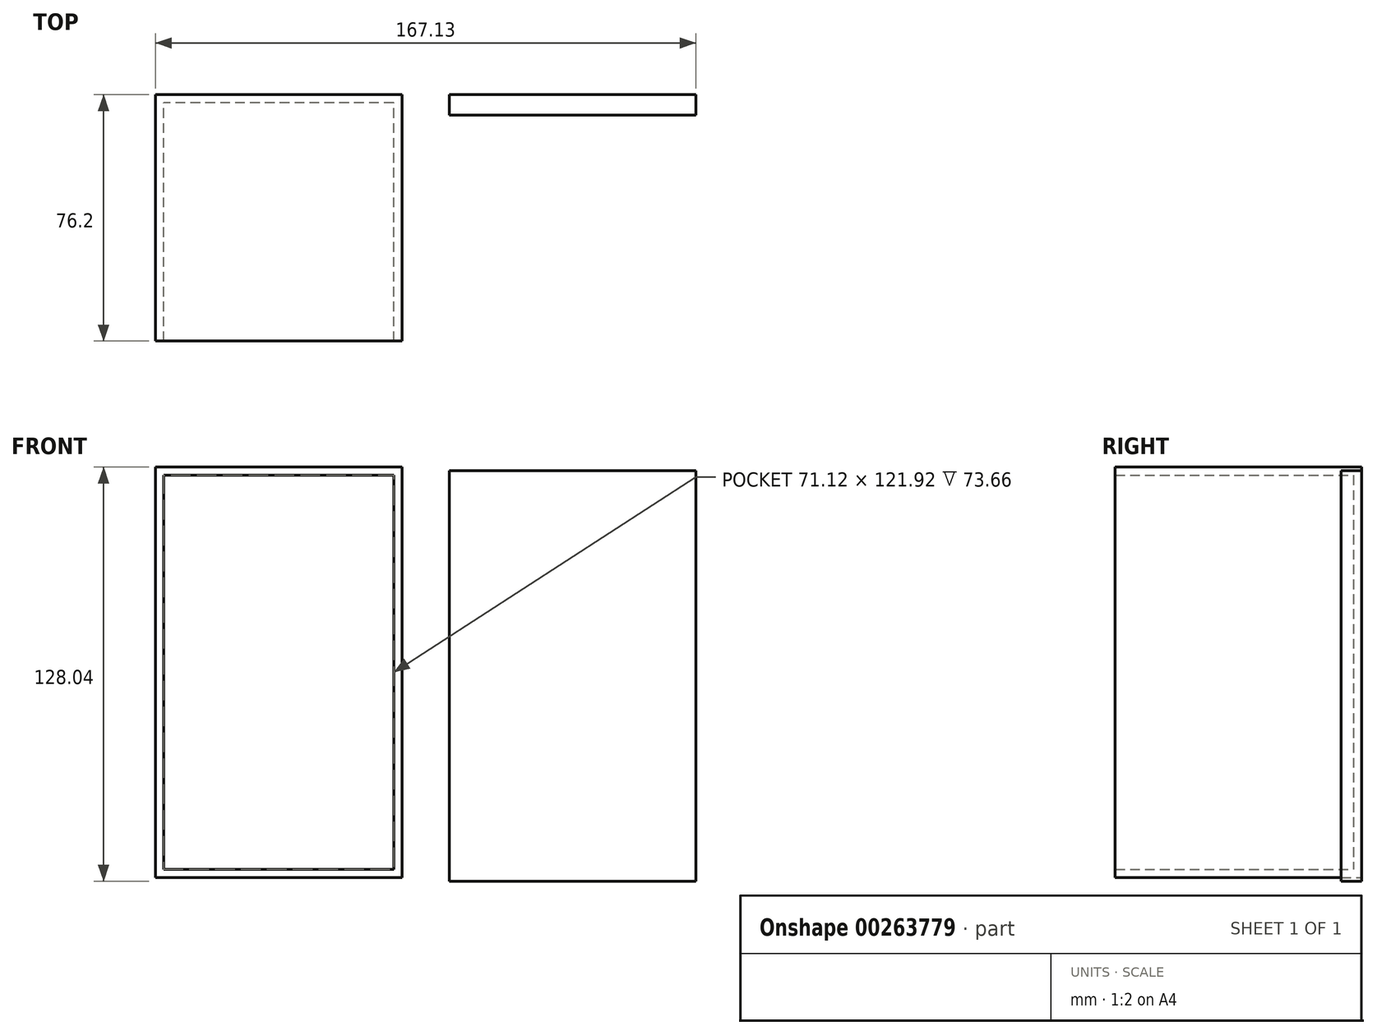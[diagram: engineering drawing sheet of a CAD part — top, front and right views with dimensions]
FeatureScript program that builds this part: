
annotation { "Feature Type Name" : "Feature", "Feature Type Description" : "" }
export const myFeature = defineFeature(function(context is Context, id is Id, definition is map)
    precondition{}
    {
        {
            var Q0;
            Q0=qCreatedBy(makeId("Front.planeOp"),FACE);
            var sketch = newSketch(context, id + "F0", { "sketchPlane" : qUnion([Q0])});
            skLineSegment(sketch, "E0.bottom", {"start": v(38.1, 63.5) * mm, "end": v(-38.1, 63.5) * mm});
            skLineSegment(sketch, "E0.top", {"start": v(38.1, -63.5) * mm, "end": v(-38.1, -63.5) * mm});
            skLineSegment(sketch, "E0.left", {"start": v(38.1, 63.5) * mm, "end": v(38.1, -63.5) * mm});
            skLineSegment(sketch, "E0.right", {"start": v(-38.1, 63.5) * mm, "end": v(-38.1, -63.5) * mm});
            skPoint(sketch, "E0.middle", {"position": v(0, 0) * mm});
            skLineSegment(sketch, "E1.bottom", {"start": v(52.83, 62.46) * mm, "end": v(129.03, 62.46) * mm});
            skLineSegment(sketch, "E1.top", {"start": v(52.83, -64.54) * mm, "end": v(129.03, -64.54) * mm});
            skLineSegment(sketch, "E1.left", {"start": v(52.83, 62.46) * mm, "end": v(52.83, -64.54) * mm});
            skLineSegment(sketch, "E1.right", {"start": v(129.03, 62.46) * mm, "end": v(129.03, -64.54) * mm});
            skSolve(sketch);
        }
        {
            var Q0;
            Q0=makeQuery(id+"F0.imprint","IMPRINT",FACE,{"disambiguationData":[TD([[makeQuery(id+"F0.imprint","IMPRINT",EDGE,{"derivedFrom":sQuery(id+"F0.wireOp",EDGE,"E0.bottom")}),1.0]])]});
            extrude(context, id + "F1", {"entities" : qUnion([Q0]), "depth" : 76.2 * mm});
        }
        {
            var Q0;
            Q0=makeQuery(id+"F0.imprint","IMPRINT",FACE,{"disambiguationData":[TD([[makeQuery(id+"F0.imprint","IMPRINT",EDGE,{"derivedFrom":sQuery(id+"F0.wireOp",EDGE,"E1.bottom")}),-1.0]])]});
            extrude(context, id + "F2", {"entities" : qUnion([Q0]), "depth" : 6.35 * mm});
        }
        {
            var Q0;
            Q0=makeQuery(id+"F1.opExtrude","CAP_FACE",FACE,{"disambiguationData":[OSD([sQuery(id+"F0.wireOp",EDGE,"E0.bottom"),sQuery(id+"F0.wireOp",EDGE,"E0.top"),sQuery(id+"F0.wireOp",EDGE,"E0.left"),sQuery(id+"F0.wireOp",EDGE,"E0.right")])],"isStart":false});
            shell(context, id + "F3", {"entities" : qUnion([Q0]), "thickness" : 2.54 * mm});
        }
    });
